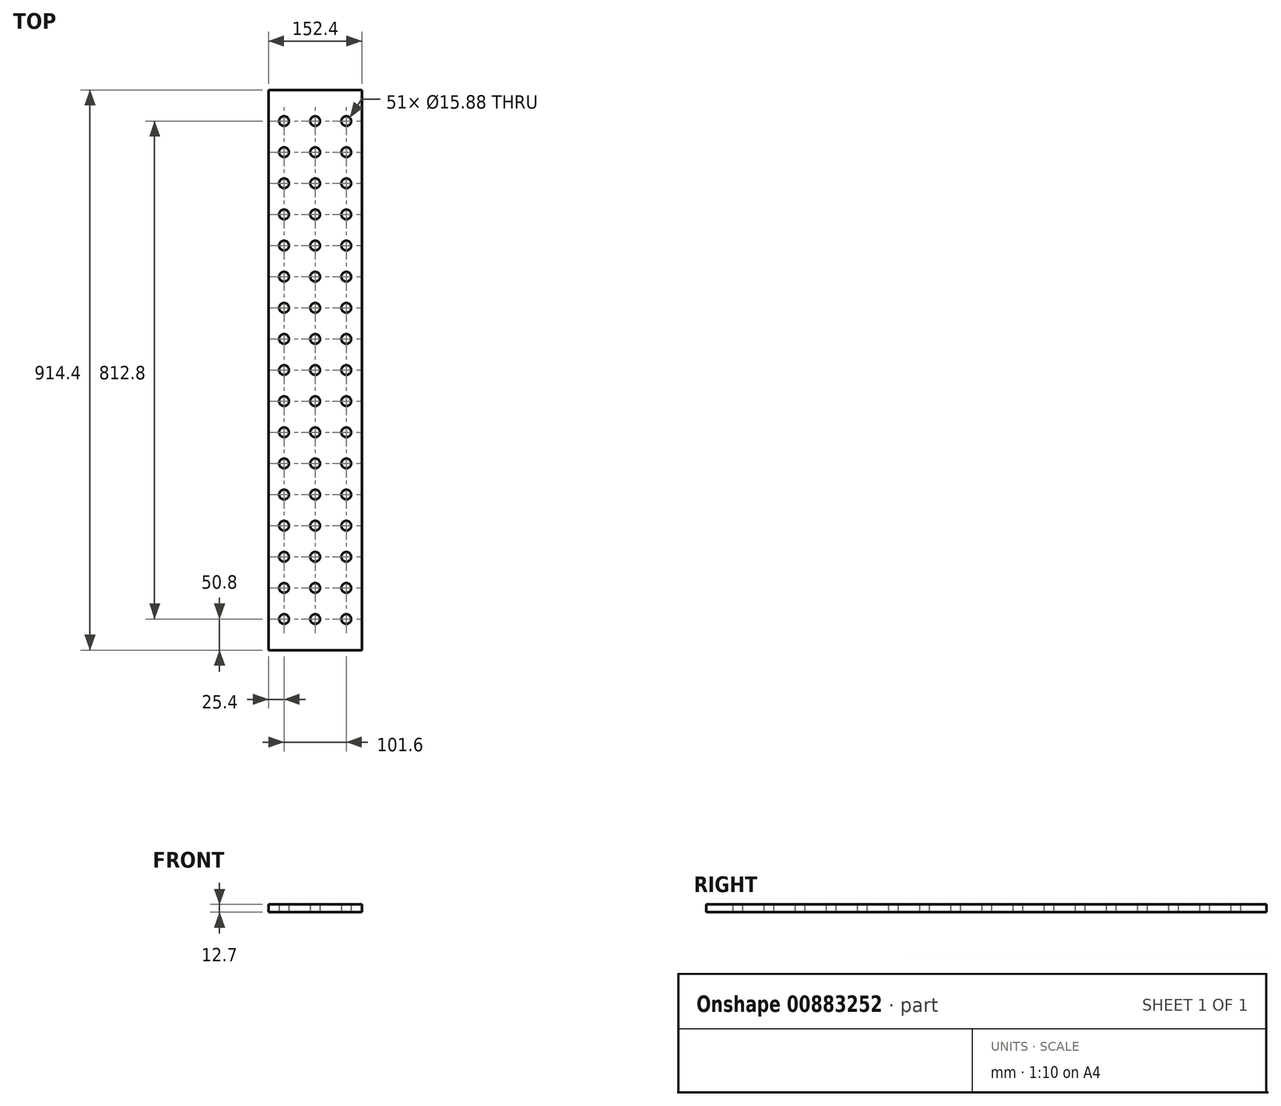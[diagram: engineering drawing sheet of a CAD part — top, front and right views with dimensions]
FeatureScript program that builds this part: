
annotation { "Feature Type Name" : "Feature", "Feature Type Description" : "" }
export const myFeature = defineFeature(function(context is Context, id is Id, definition is map)
    precondition{}
    {
        {
            var Q0;
            Q0=qCreatedBy(makeId("Top.planeOp"),FACE);
            var sketch = newSketch(context, id + "F0", { "sketchPlane" : qUnion([Q0])});
            skCircle(sketch, "E0.0.1.0", {"center": v(0, 50.8) * mm, "radius": 7.94 * mm});
            skCircle(sketch, "E0.0.2.0", {"center": v(0, 101.6) * mm, "radius": 7.94 * mm});
            skCircle(sketch, "E0.0.3.0", {"center": v(0, 152.4) * mm, "radius": 7.94 * mm});
            skCircle(sketch, "E0.0.4.0", {"center": v(0, 203.2) * mm, "radius": 7.94 * mm});
            skCircle(sketch, "E0.0.5.0", {"center": v(0, 254) * mm, "radius": 7.94 * mm});
            skCircle(sketch, "E0.0.6.0", {"center": v(0, 304.8) * mm, "radius": 7.94 * mm});
            skCircle(sketch, "E0.0.7.0", {"center": v(0, 355.6) * mm, "radius": 7.94 * mm});
            skCircle(sketch, "E0.0.8.0", {"center": v(0, 406.4) * mm, "radius": 7.94 * mm});
            skCircle(sketch, "E0.0.9.0", {"center": v(0, 457.2) * mm, "radius": 7.94 * mm});
            skCircle(sketch, "E0.0.10.0", {"center": v(0, 508) * mm, "radius": 7.94 * mm});
            skCircle(sketch, "E0.0.11.0", {"center": v(0, 558.8) * mm, "radius": 7.94 * mm});
            skCircle(sketch, "E0.0.12.0", {"center": v(0, 609.6) * mm, "radius": 7.94 * mm});
            skCircle(sketch, "E0.0.13.0", {"center": v(0, 660.4) * mm, "radius": 7.94 * mm});
            skCircle(sketch, "E0.0.14.0", {"center": v(0, 711.2) * mm, "radius": 7.94 * mm});
            skCircle(sketch, "E0.0.15.0", {"center": v(0, 762) * mm, "radius": 7.94 * mm});
            skCircle(sketch, "E0.0.16.0", {"center": v(0, 812.8) * mm, "radius": 7.94 * mm});
            skCircle(sketch, "E0.0.17.0", {"center": v(0, 863.6) * mm, "radius": 7.94 * mm});
            skCircle(sketch, "E0.1.1.0", {"center": v(50.8, 50.8) * mm, "radius": 7.94 * mm});
            skCircle(sketch, "E0.1.2.0", {"center": v(50.8, 101.6) * mm, "radius": 7.94 * mm});
            skCircle(sketch, "E0.1.3.0", {"center": v(50.8, 152.4) * mm, "radius": 7.94 * mm});
            skCircle(sketch, "E0.1.4.0", {"center": v(50.8, 203.2) * mm, "radius": 7.94 * mm});
            skCircle(sketch, "E0.1.5.0", {"center": v(50.8, 254) * mm, "radius": 7.94 * mm});
            skCircle(sketch, "E0.1.6.0", {"center": v(50.8, 304.8) * mm, "radius": 7.94 * mm});
            skCircle(sketch, "E0.1.7.0", {"center": v(50.8, 355.6) * mm, "radius": 7.94 * mm});
            skCircle(sketch, "E0.1.8.0", {"center": v(50.8, 406.4) * mm, "radius": 7.94 * mm});
            skCircle(sketch, "E0.1.9.0", {"center": v(50.8, 457.2) * mm, "radius": 7.94 * mm});
            skCircle(sketch, "E0.1.10.0", {"center": v(50.8, 508) * mm, "radius": 7.94 * mm});
            skCircle(sketch, "E0.1.11.0", {"center": v(50.8, 558.8) * mm, "radius": 7.94 * mm});
            skCircle(sketch, "E0.1.12.0", {"center": v(50.8, 609.6) * mm, "radius": 7.94 * mm});
            skCircle(sketch, "E0.1.13.0", {"center": v(50.8, 660.4) * mm, "radius": 7.94 * mm});
            skCircle(sketch, "E0.1.14.0", {"center": v(50.8, 711.2) * mm, "radius": 7.94 * mm});
            skCircle(sketch, "E0.1.15.0", {"center": v(50.8, 762) * mm, "radius": 7.94 * mm});
            skCircle(sketch, "E0.1.16.0", {"center": v(50.8, 812.8) * mm, "radius": 7.94 * mm});
            skCircle(sketch, "E0.1.17.0", {"center": v(50.8, 863.6) * mm, "radius": 7.94 * mm});
            skCircle(sketch, "E0.2.1.0", {"center": v(101.6, 50.8) * mm, "radius": 7.94 * mm});
            skCircle(sketch, "E0.2.2.0", {"center": v(101.6, 101.6) * mm, "radius": 7.94 * mm});
            skCircle(sketch, "E0.2.3.0", {"center": v(101.6, 152.4) * mm, "radius": 7.94 * mm});
            skCircle(sketch, "E0.2.4.0", {"center": v(101.6, 203.2) * mm, "radius": 7.94 * mm});
            skCircle(sketch, "E0.2.5.0", {"center": v(101.6, 254) * mm, "radius": 7.94 * mm});
            skCircle(sketch, "E0.2.6.0", {"center": v(101.6, 304.8) * mm, "radius": 7.94 * mm});
            skCircle(sketch, "E0.2.7.0", {"center": v(101.6, 355.6) * mm, "radius": 7.94 * mm});
            skCircle(sketch, "E0.2.8.0", {"center": v(101.6, 406.4) * mm, "radius": 7.94 * mm});
            skCircle(sketch, "E0.2.9.0", {"center": v(101.6, 457.2) * mm, "radius": 7.94 * mm});
            skCircle(sketch, "E0.2.10.0", {"center": v(101.6, 508) * mm, "radius": 7.94 * mm});
            skCircle(sketch, "E0.2.11.0", {"center": v(101.6, 558.8) * mm, "radius": 7.94 * mm});
            skCircle(sketch, "E0.2.12.0", {"center": v(101.6, 609.6) * mm, "radius": 7.94 * mm});
            skCircle(sketch, "E0.2.13.0", {"center": v(101.6, 660.4) * mm, "radius": 7.94 * mm});
            skCircle(sketch, "E0.2.14.0", {"center": v(101.6, 711.2) * mm, "radius": 7.94 * mm});
            skCircle(sketch, "E0.2.15.0", {"center": v(101.6, 762) * mm, "radius": 7.94 * mm});
            skCircle(sketch, "E0.2.16.0", {"center": v(101.6, 812.8) * mm, "radius": 7.94 * mm});
            skCircle(sketch, "E0.2.17.0", {"center": v(101.6, 863.6) * mm, "radius": 7.94 * mm});
            skLineSegment(sketch, "E1.bottom", {"start": v(-25.4, 914.4) * mm, "end": v(127, 914.4) * mm});
            skLineSegment(sketch, "E1.left", {"start": v(-25.4, 914.4) * mm, "end": v(-25.4, 0) * mm});
            skLineSegment(sketch, "E1.right", {"start": v(127, 914.4) * mm, "end": v(127, 0) * mm});
            skLineSegment(sketch, "E2", {"start": v(-25.4, 0) * mm, "end": v(127, 0) * mm});
            skSolve(sketch);
        }
        {
            var Q0;
            Q0=makeQuery(id+"F0.imprint","IMPRINT",FACE,{"disambiguationData":[TD([[makeQuery(id+"F0.imprint","IMPRINT",EDGE,{"derivedFrom":sQuery(id+"F0.wireOp",EDGE,"E0.0.1.0")}),-1.0]])]});
            extrude(context, id + "F1", {"entities" : qUnion([Q0]), "depth" : 12.7 * mm, "offsetDistance" : 25.4 * mm});
        }
    });
